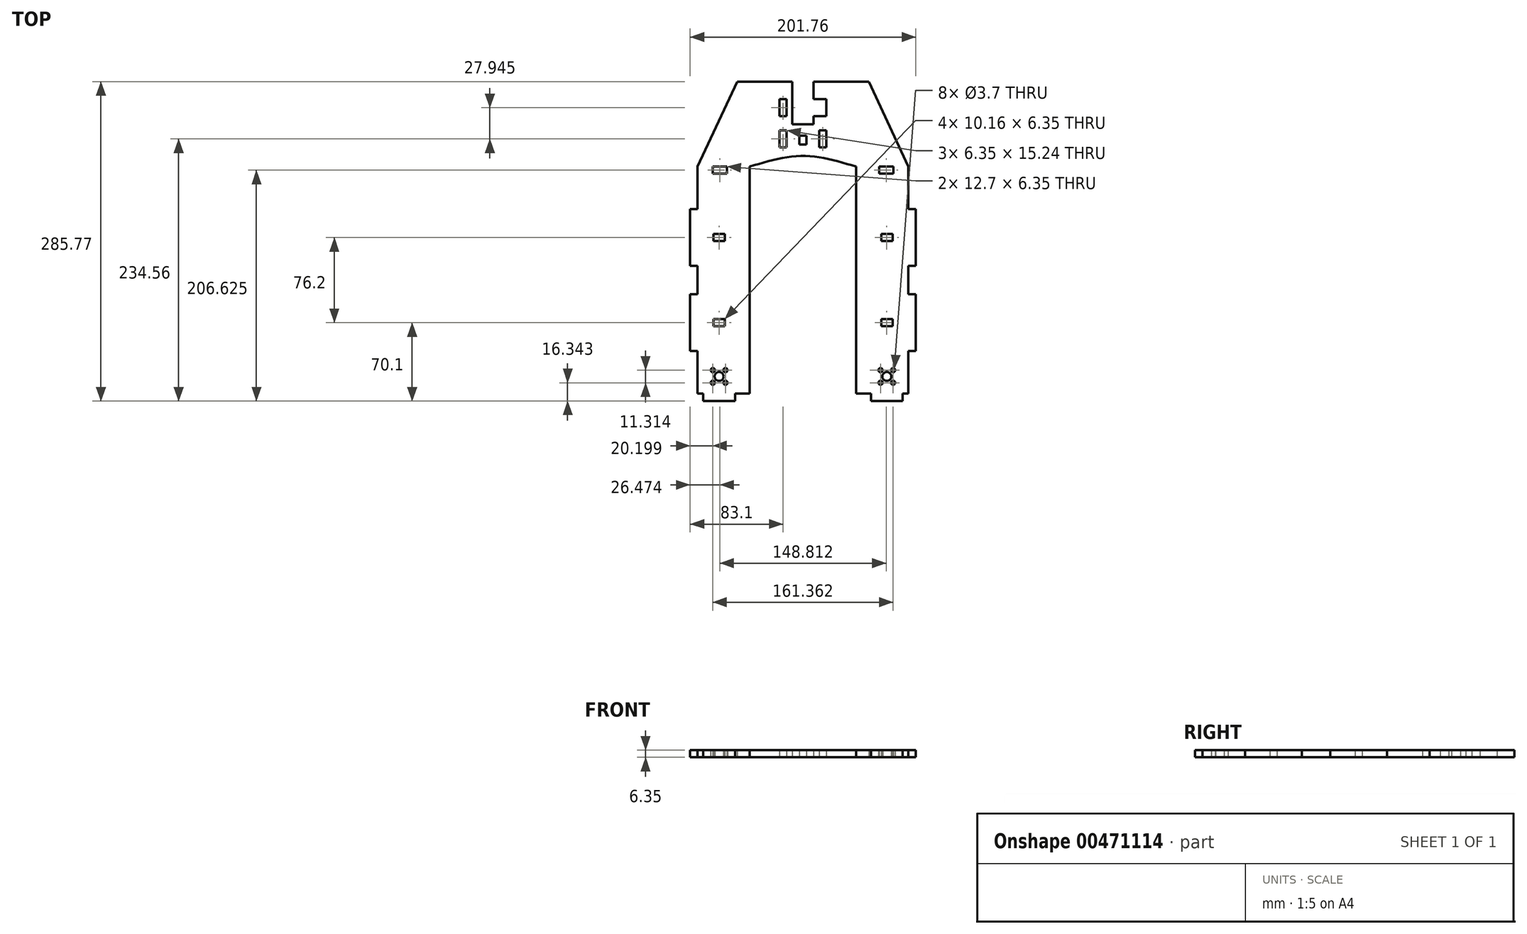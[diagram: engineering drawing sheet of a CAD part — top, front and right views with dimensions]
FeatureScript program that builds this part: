
annotation { "Feature Type Name" : "Feature", "Feature Type Description" : "" }
export const myFeature = defineFeature(function(context is Context, id is Id, definition is map)
    precondition{}
    {
        {
            var Q0;
            Q0=qCreatedBy(makeId("Top.planeOp"),FACE);
            var sketch = newSketch(context, id + "F0", { "sketchPlane" : qUnion([Q0])});
            skLineSegment(sketch, "E0", {"start": v(-60.85, 0) * mm, "end": v(-60.85, -6.6) * mm});
            skLineSegment(sketch, "E1", {"start": v(-60.85, -6.6) * mm, "end": v(-89.2, -6.6) * mm});
            skLineSegment(sketch, "E2", {"start": v(-89.2, -6.6) * mm, "end": v(-89.2, 0) * mm});
            skLineSegment(sketch, "E3", {"start": v(-89.2, 0) * mm, "end": v(-94.28, 0) * mm});
            skLineSegment(sketch, "E4", {"start": v(-94.28, 0) * mm, "end": v(-94.28, 38.1) * mm});
            skLineSegment(sketch, "E5", {"start": v(-94.28, 38.1) * mm, "end": v(-100.88, 38.1) * mm});
            skLineSegment(sketch, "E6", {"start": v(-100.88, 38.1) * mm, "end": v(-100.88, 88.9) * mm});
            skLineSegment(sketch, "E7", {"start": v(-100.88, 88.9) * mm, "end": v(-94.28, 88.9) * mm});
            skLineSegment(sketch, "E8", {"start": v(-94.28, 165.1) * mm, "end": v(-100.88, 165.1) * mm});
            skLineSegment(sketch, "E9", {"start": v(-100.88, 165.1) * mm, "end": v(-100.88, 114.3) * mm});
            skLineSegment(sketch, "E10", {"start": v(-100.88, 114.3) * mm, "end": v(-94.28, 114.3) * mm});
            skLineSegment(sketch, "E11.trimOffspring", {"start": v(-94.28, 165.1) * mm, "end": v(-94.28, 203.2) * mm});
            skLineSegment(sketch, "E12.trimOffspring", {"start": v(-94.28, 88.9) * mm, "end": v(-94.28, 114.3) * mm});
            skCircle(sketch, "E13", {"center": v(-75.02, 15.4) * mm, "radius": 4 * mm});
            skCircle(sketch, "E14.1.0", {"center": v(-80.68, 9.74) * mm, "radius": 1.85 * mm});
            skCircle(sketch, "E15.1.3.0", {"center": v(-69.37, 9.74) * mm, "radius": 1.85 * mm});
            skCircle(sketch, "E15.1.5.0", {"center": v(-69.37, 21.06) * mm, "radius": 1.85 * mm});
            skCircle(sketch, "E15.1.7.0", {"center": v(-80.68, 21.06) * mm, "radius": 1.85 * mm});
            skLineSegment(sketch, "E16", {"start": v(-80.76, 203.2) * mm, "end": v(-80.76, 196.85) * mm});
            skLineSegment(sketch, "E17", {"start": v(-80.76, 196.85) * mm, "end": v(-68.06, 196.85) * mm});
            skLineSegment(sketch, "E18", {"start": v(-68.06, 196.85) * mm, "end": v(-68.06, 203.2) * mm});
            skLineSegment(sketch, "E19", {"start": v(-80.76, 203.2) * mm, "end": v(-68.06, 203.2) * mm});
            skLineSegment(sketch, "E20", {"start": v(0, 0) * mm, "end": v(0, 212.73) * mm, "construction": true});
            skLineSegment(sketch, "E21", {"start": v(-58.85, 279.17) * mm, "end": v(-9.53, 279.17) * mm});
            skLineSegment(sketch, "E22", {"start": v(-94.28, 203.2) * mm, "end": v(-58.85, 279.17) * mm});
            skLineSegment(sketch, "E23", {"start": v(-9.53, 279.17) * mm, "end": v(-9.53, 241.07) * mm});
            skLineSegment(sketch, "E24.MirrorCS", {"start": v(94.28, 203.2) * mm, "end": v(58.85, 279.17) * mm});
            skLineSegment(sketch, "E25.MirrorCS", {"start": v(9.53, 279.17) * mm, "end": v(9.53, 263.53) * mm});
            skLineSegment(sketch, "E26.MirrorCS", {"start": v(58.85, 279.17) * mm, "end": v(9.53, 279.17) * mm});
            skLineSegment(sketch, "E27.MirrorCS", {"start": v(80.76, 203.2) * mm, "end": v(80.76, 196.85) * mm});
            skCircle(sketch, "E28.MirrorC", {"center": v(69.37, 9.74) * mm, "radius": 1.85 * mm});
            skCircle(sketch, "E29.MirrorC", {"center": v(69.37, 21.06) * mm, "radius": 1.85 * mm});
            skLineSegment(sketch, "E30.MirrorCS", {"start": v(80.76, 196.85) * mm, "end": v(68.06, 196.85) * mm});
            skLineSegment(sketch, "E31.MirrorCS", {"start": v(100.88, 114.3) * mm, "end": v(94.28, 114.3) * mm});
            skCircle(sketch, "E32.MirrorC", {"center": v(75.02, 15.4) * mm, "radius": 4 * mm});
            skLineSegment(sketch, "E33.MirrorCS", {"start": v(89.2, -6.6) * mm, "end": v(89.2, 0) * mm});
            skLineSegment(sketch, "E34.MirrorCS", {"start": v(60.85, 0) * mm, "end": v(60.85, -6.6) * mm});
            skLineSegment(sketch, "E35.MirrorCS", {"start": v(80.76, 203.2) * mm, "end": v(68.06, 203.2) * mm});
            skLineSegment(sketch, "E36.MirrorCS", {"start": v(94.28, 38.1) * mm, "end": v(100.88, 38.1) * mm});
            skLineSegment(sketch, "E37.MirrorCS", {"start": v(100.88, 88.9) * mm, "end": v(94.28, 88.9) * mm});
            skLineSegment(sketch, "E38.MirrorCS", {"start": v(94.28, 165.1) * mm, "end": v(100.88, 165.1) * mm});
            skLineSegment(sketch, "E39.MirrorCS", {"start": v(68.06, 196.85) * mm, "end": v(68.06, 203.2) * mm});
            skLineSegment(sketch, "E40.MirrorCS", {"start": v(89.2, 0) * mm, "end": v(94.28, 0) * mm});
            skCircle(sketch, "E41.MirrorC", {"center": v(80.68, 9.74) * mm, "radius": 1.85 * mm});
            skCircle(sketch, "E42.MirrorC", {"center": v(80.68, 21.06) * mm, "radius": 1.85 * mm});
            skLineSegment(sketch, "E43.MirrorCS", {"start": v(60.85, -6.6) * mm, "end": v(89.2, -6.6) * mm});
            skLineSegment(sketch, "E44.MirrorCS", {"start": v(94.28, 165.1) * mm, "end": v(94.28, 203.2) * mm});
            skLineSegment(sketch, "E45.MirrorCS", {"start": v(94.28, 88.9) * mm, "end": v(94.28, 114.3) * mm});
            skLineSegment(sketch, "E46.MirrorCS", {"start": v(94.28, 0) * mm, "end": v(94.28, 38.1) * mm});
            skLineSegment(sketch, "E47.MirrorCS", {"start": v(100.88, 38.1) * mm, "end": v(100.88, 88.9) * mm});
            skLineSegment(sketch, "E48.MirrorCS", {"start": v(100.88, 165.1) * mm, "end": v(100.88, 114.3) * mm});
            skLineSegment(sketch, "E49", {"start": v(-9.53, 241.07) * mm, "end": v(9.53, 241.07) * mm});
            skLineSegment(sketch, "E50", {"start": v(14.6, 235.58) * mm, "end": v(20.96, 235.58) * mm});
            skLineSegment(sketch, "E51", {"start": v(20.96, 235.58) * mm, "end": v(20.96, 220.34) * mm});
            skLineSegment(sketch, "E52", {"start": v(20.96, 220.34) * mm, "end": v(14.6, 220.34) * mm});
            skLineSegment(sketch, "E53", {"start": v(14.6, 220.34) * mm, "end": v(14.6, 235.58) * mm});
            skLineSegment(sketch, "E54", {"start": v(20.96, 263.53) * mm, "end": v(20.96, 248.29) * mm});
            skLineSegment(sketch, "E55.MirrorCS", {"start": v(-20.96, 235.58) * mm, "end": v(-20.96, 220.34) * mm});
            skLineSegment(sketch, "E56.MirrorCS", {"start": v(-14.6, 235.58) * mm, "end": v(-20.96, 235.58) * mm});
            skLineSegment(sketch, "E57.MirrorCS", {"start": v(-20.96, 220.34) * mm, "end": v(-14.6, 220.34) * mm});
            skLineSegment(sketch, "E58.MirrorCS", {"start": v(-20.96, 248.29) * mm, "end": v(-14.6, 248.29) * mm});
            skLineSegment(sketch, "E59.MirrorCS", {"start": v(-14.6, 220.34) * mm, "end": v(-14.6, 235.58) * mm});
            skLineSegment(sketch, "E60.MirrorCS", {"start": v(-14.6, 248.29) * mm, "end": v(-14.6, 263.53) * mm});
            skLineSegment(sketch, "E61.MirrorCS", {"start": v(-14.6, 263.53) * mm, "end": v(-20.96, 263.53) * mm});
            skLineSegment(sketch, "E62.MirrorCS", {"start": v(-20.96, 263.53) * mm, "end": v(-20.96, 248.29) * mm});
            skLineSegment(sketch, "E63.trimOffspring", {"start": v(9.53, 248.29) * mm, "end": v(9.53, 241.07) * mm});
            skLineSegment(sketch, "E64", {"start": v(9.53, 263.53) * mm, "end": v(20.96, 263.53) * mm});
            skLineSegment(sketch, "E65", {"start": v(9.53, 248.29) * mm, "end": v(20.96, 248.29) * mm});
            skPoint(sketch, "E66.endSnap0", {"position": v(0, 241.07) * mm});
            skLineSegment(sketch, "E67", {"start": v(3.18, 230.9) * mm, "end": v(3.18, 222.89) * mm});
            skLineSegment(sketch, "E68.MirrorCS", {"start": v(-3.18, 230.9) * mm, "end": v(-3.18, 222.89) * mm});
            skLineSegment(sketch, "E69", {"start": v(-3.18, 222.89) * mm, "end": v(3.18, 222.89) * mm});
            skLineSegment(sketch, "E70", {"start": v(-3.18, 230.9) * mm, "end": v(3.18, 230.9) * mm});
            skLineSegment(sketch, "E71", {"start": v(-75.02, 15.4) * mm, "end": v(-75.02, 174.62) * mm, "construction": true});
            skLineSegment(sketch, "E72", {"start": v(-100.88, 139.7) * mm, "end": v(-54.53, 139.7) * mm, "construction": true});
            skLineSegment(sketch, "E73", {"start": v(-80.1, 142.88) * mm, "end": v(-69.94, 142.88) * mm});
            skLineSegment(sketch, "E74.MirrorCS", {"start": v(-80.1, 136.53) * mm, "end": v(-69.94, 136.53) * mm});
            skLineSegment(sketch, "E75", {"start": v(-80.1, 142.88) * mm, "end": v(-80.1, 136.53) * mm});
            skLineSegment(sketch, "E76", {"start": v(-69.94, 142.88) * mm, "end": v(-69.94, 136.53) * mm});
            skLineSegment(sketch, "E77", {"start": v(-94.28, 101.6) * mm, "end": v(-54.53, 101.6) * mm, "construction": true});
            skLineSegment(sketch, "E78.MirrorCS", {"start": v(-80.1, 66.68) * mm, "end": v(-69.94, 66.68) * mm});
            skLineSegment(sketch, "E79.MirrorCS", {"start": v(-80.1, 60.32) * mm, "end": v(-69.94, 60.32) * mm});
            skLineSegment(sketch, "E80.MirrorCS", {"start": v(-69.94, 60.32) * mm, "end": v(-69.94, 66.68) * mm});
            skLineSegment(sketch, "E81.MirrorCS", {"start": v(-80.1, 60.32) * mm, "end": v(-80.1, 66.68) * mm});
            skLineSegment(sketch, "E82.MirrorCS", {"start": v(80.1, 142.88) * mm, "end": v(69.94, 142.88) * mm});
            skLineSegment(sketch, "E83.MirrorCS", {"start": v(80.1, 142.88) * mm, "end": v(80.1, 136.53) * mm});
            skLineSegment(sketch, "E84.MirrorCS", {"start": v(80.1, 136.53) * mm, "end": v(69.94, 136.53) * mm});
            skLineSegment(sketch, "E85.MirrorCS", {"start": v(69.94, 142.88) * mm, "end": v(69.94, 136.53) * mm});
            skLineSegment(sketch, "E86.MirrorCS", {"start": v(80.1, 66.68) * mm, "end": v(69.94, 66.68) * mm});
            skLineSegment(sketch, "E87.MirrorCS", {"start": v(69.94, 60.32) * mm, "end": v(69.94, 66.68) * mm});
            skLineSegment(sketch, "E88.MirrorCS", {"start": v(80.1, 60.32) * mm, "end": v(69.94, 60.32) * mm});
            skLineSegment(sketch, "E89.MirrorCS", {"start": v(80.1, 60.32) * mm, "end": v(80.1, 66.68) * mm});
            skLineSegment(sketch, "E90", {"start": v(-47.63, 0) * mm, "end": v(-47.63, 203.2) * mm});
            skLineSegment(sketch, "E91", {"start": v(-60.85, 0) * mm, "end": v(-47.63, 0) * mm});
            skLineSegment(sketch, "E92.MirrorCS", {"start": v(47.63, 0) * mm, "end": v(47.63, 203.2) * mm});
            skLineSegment(sketch, "E93.MirrorCS", {"start": v(60.85, 0) * mm, "end": v(47.63, 0) * mm});
            skFitSpline(sketch, "E94", {"points": [v(-47.63, 203.2) * mm, v(0, 212.73) * mm, v(47.63, 203.2) * mm], "startDerivative": vector(95.25, 28.57) * mm, "endDerivative": vector(95.25, -28.58) * mm});
            skSolve(sketch);
        }
        {
            var Q0;
            Q0=makeQuery(id+"F0.imprint","IMPRINT",FACE,{"disambiguationData":[TD([[makeQuery(id+"F0.imprint","IMPRINT",EDGE,{"derivedFrom":sQuery(id+"F0.wireOp",EDGE,"E0")}),-1.0]])]});
            extrude(context, id + "F1", {"entities" : qUnion([Q0]), "depth" : 6.35 * mm});
        }
    });
